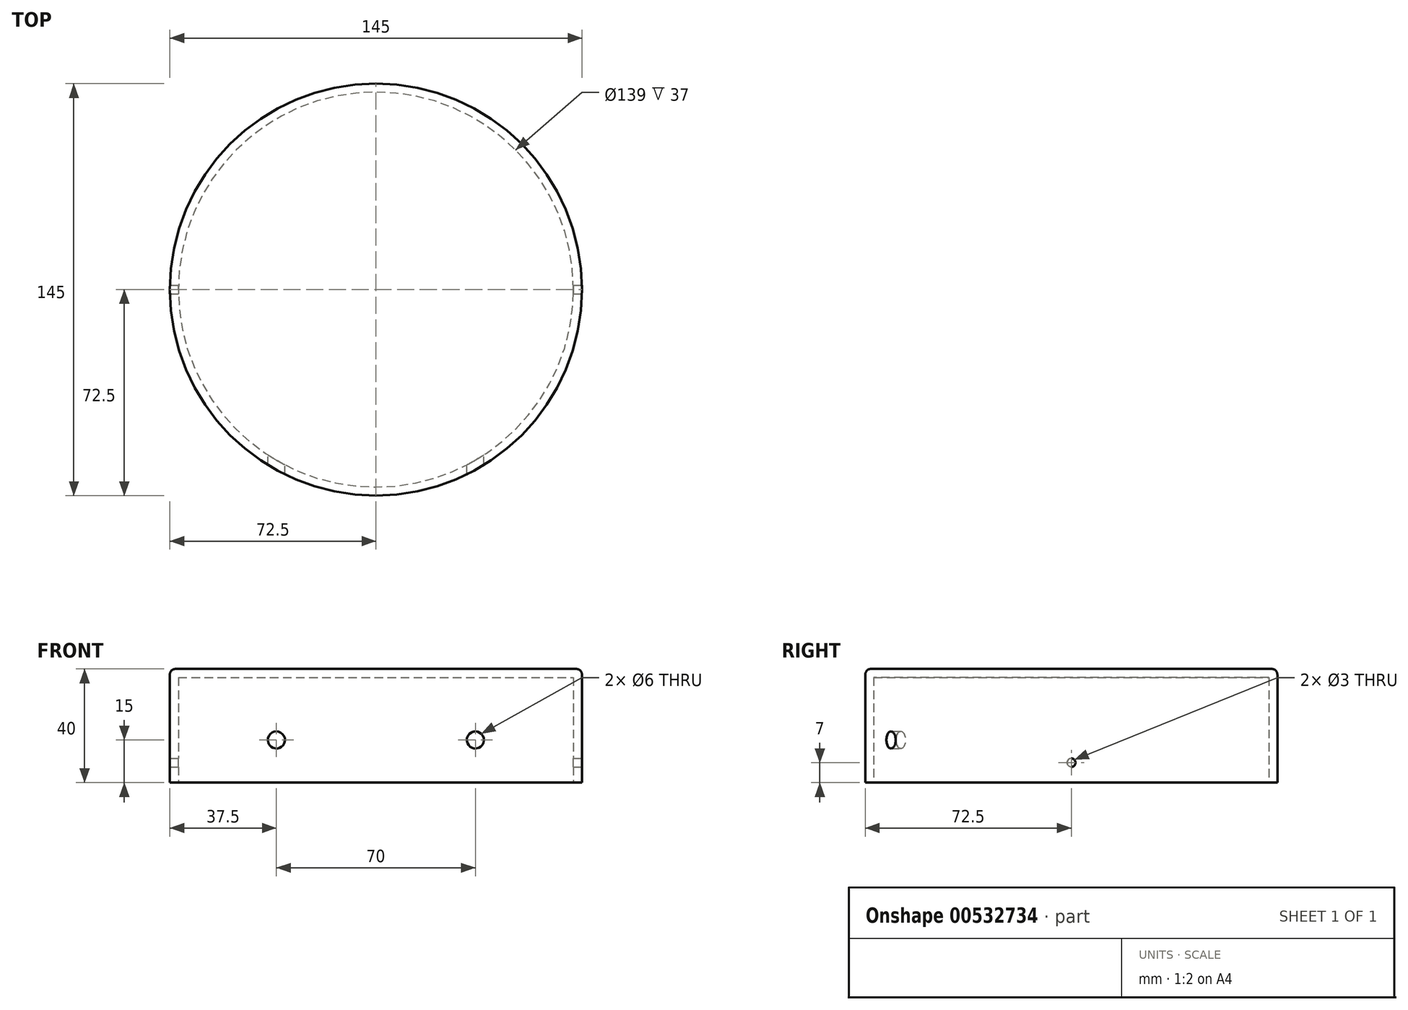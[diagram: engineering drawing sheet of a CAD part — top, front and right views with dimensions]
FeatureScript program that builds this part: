
annotation { "Feature Type Name" : "Feature", "Feature Type Description" : "" }
export const myFeature = defineFeature(function(context is Context, id is Id, definition is map)
    precondition{}
    {
        {
            var Q0;
            Q0=qCreatedBy(makeId("Top.planeOp"),FACE);
            var sketch = newSketch(context, id + "F0", { "sketchPlane" : qUnion([Q0])});
            skCircle(sketch, "E0", {"center": v(0, 0) * mm, "radius": 72.5 * mm});
            skSolve(sketch);
        }
        {
            var Q0;
            Q0 = qSketchRegion(id + "F0", true);
            extrude(context, id + "F1", {"entities" : qUnion([Q0]), "depth" : 40 * mm, "offsetDistance" : 25 * mm});
        }
        {
            var Q0;
            Q0=makeQuery(id+"F1.opExtrude","CAP_FACE",FACE,{"disambiguationData":[OSD([sQuery(id+"F0.wireOp",EDGE,"E0")])],"isStart":true});
            var sketch = newSketch(context, id + "F2", { "sketchPlane" : qUnion([Q0])});
            skCircle(sketch, "E1", {"center": v(0, 0) * mm, "radius": 69.5 * mm});
            skSolve(sketch);
        }
        {
            var Q0;
            Q0 = qSketchRegion(id + "F2", true);
            extrude(context, id + "F3", {"entities" : qUnion([Q0]), "operationType" : NewBodyOperationType.REMOVE, "oppositeDirection" : true, "depth" : 37 * mm, "offsetDistance" : 25 * mm});
        }
        {
            var Q0;
            Q0=qCreatedBy(makeId("Front.planeOp"),FACE);
            var sketch = newSketch(context, id + "F4", { "sketchPlane" : qUnion([Q0])});
            skCircle(sketch, "E2", {"center": v(35, 15) * mm, "radius": 3 * mm});
            skCircle(sketch, "E3", {"center": v(-35, 15) * mm, "radius": 3 * mm});
            skLineSegment(sketch, "E4", {"start": v(-35, 15) * mm, "end": v(35, 15) * mm, "construction": true});
            skLineSegment(sketch, "E5", {"start": v(0, 0) * mm, "end": v(0, 15) * mm, "construction": true});
            skSolve(sketch);
        }
        {
            var Q0;
            Q0 = qSketchRegion(id + "F4", true);
            extrude(context, id + "F5", {"entities" : qUnion([Q0]), "operationType" : NewBodyOperationType.REMOVE, "endBound" : BoundingType.THROUGH_ALL, "depth" : 25 * mm, "offsetDistance" : 25 * mm});
        }
        {
            var Q0;
            Q0=qCreatedBy(makeId("Right.planeOp"),FACE);
            var sketch = newSketch(context, id + "F6", { "sketchPlane" : qUnion([Q0])});
            skCircle(sketch, "E6", {"center": v(0, 7) * mm, "radius": 1.5 * mm});
            skLineSegment(sketch, "E7", {"start": v(0, 0) * mm, "end": v(0, 7) * mm, "construction": true});
            skSolve(sketch);
        }
        {
            var Q0;
            Q0 = qSketchRegion(id + "F6", true);
            extrude(context, id + "F7", {"entities" : qUnion([Q0]), "operationType" : NewBodyOperationType.REMOVE, "endBound" : BoundingType.THROUGH_ALL, "oppositeDirection" : true, "depth" : 25 * mm, "offsetDistance" : 25 * mm, "hasSecondDirection" : true, "secondDirectionBound" : SecondDirectionBoundingType.THROUGH_ALL, "secondDirectionOppositeDirection" : false, "secondDirectionDepth" : 25 * mm});
        }
        {
            var Q0;
            Q0=makeQuery(id+"F1.opExtrude","CAP_EDGE",EDGE,{"disambiguationData":[OSD([sQuery(id+"F0.wireOp",EDGE,"E0")])],"isStart":false});
            fillet(context, id + "F8", {"entities" : qUnion([Q0]), "radius" : 2 * mm, "tangentPropagation" : true, "allowEdgeOverflow" : false});
        }
    });
